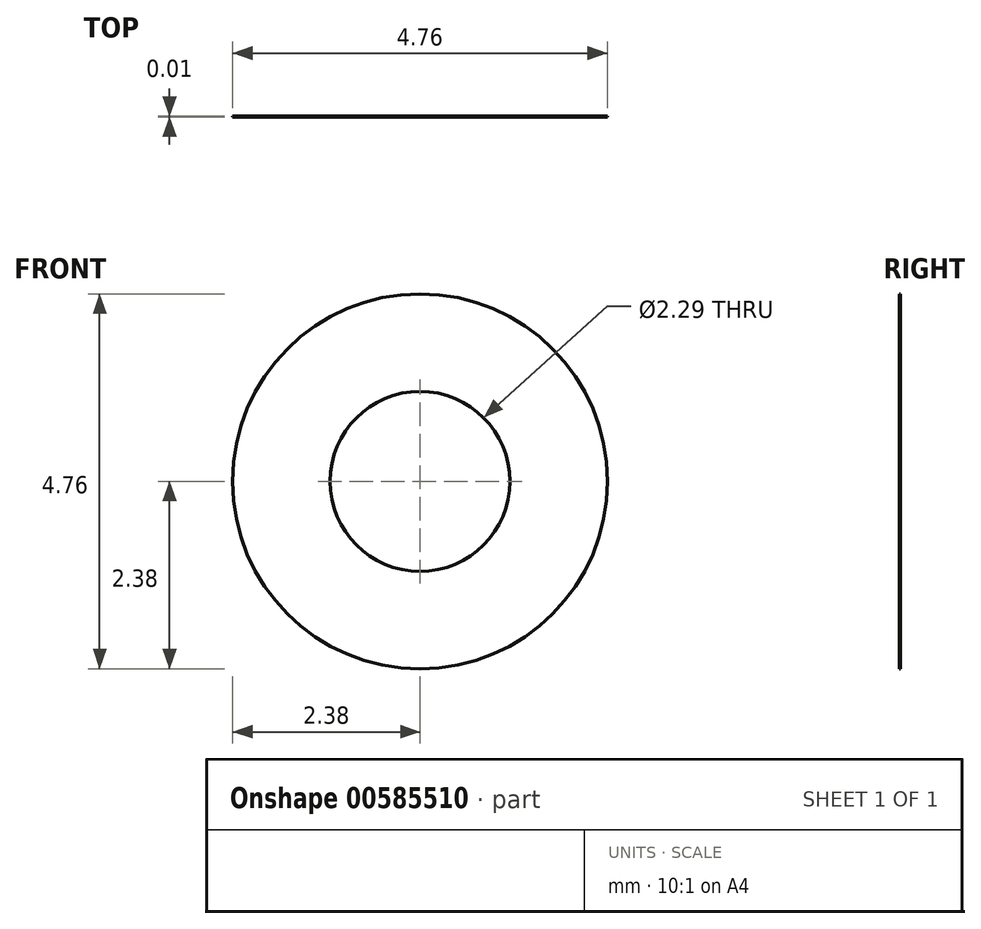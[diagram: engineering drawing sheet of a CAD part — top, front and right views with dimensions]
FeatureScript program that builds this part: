
annotation { "Feature Type Name" : "Feature", "Feature Type Description" : "" }
export const myFeature = defineFeature(function(context is Context, id is Id, definition is map)
    precondition{}
    {
        {
            var Q0;
            Q0=qCreatedBy(makeId("Front.planeOp"),FACE);
            var sketch = newSketch(context, id + "F0", { "sketchPlane" : qUnion([Q0])});
            skCircle(sketch, "E0", {"center": v(0, 0) * mm, "radius": 2.38 * mm});
            skCircle(sketch, "E1", {"center": v(0, 0) * mm, "radius": 1.14 * mm});
            skSolve(sketch);
        }
        {
            var Q0;
            Q0 = qSketchRegion(id + "F0", true);
            extrude(context, id + "F1", {"entities" : qUnion([Q0]), "depth" : 5 / 406.4 * mm, "offsetDistance" : 25 * mm});
        }
    });
